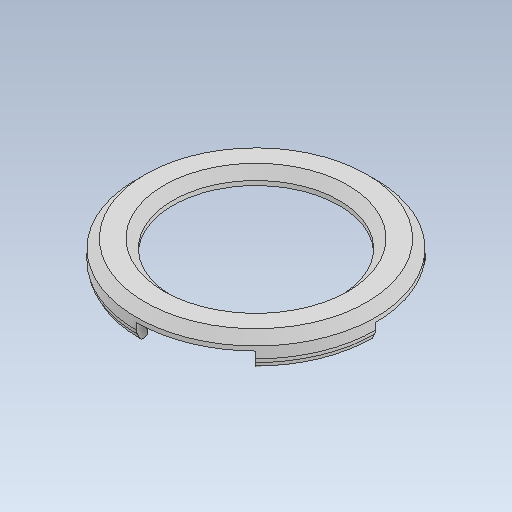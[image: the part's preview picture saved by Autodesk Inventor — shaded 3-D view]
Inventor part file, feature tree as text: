
AUTODESK INVENTOR PART (.ipt)
format: ipt  version: 2020 (Build 240168000, 168)  size: 195,584 bytes
history: native  units: mm
features: revolve x2, chamfer x2, sketch x2, other x1, pattern_circular x1
ambient origin geometry x8: Origin, YZ Plane, XZ Plane, XY Plane, X Axis, Y Axis, Z Axis, Center Point
bodies: Body1 (feature_tree)
feature tree (8):
  other  "Твердое тело1"
  revolve  "Вращение1"
  chamfer  "Фаска1"  Distance=19.0mm
  chamfer  "Фаска2"  Distance=27.3mm
  revolve  "Вращение2"
  pattern_circular  "Круговой массив1"  [2 undecoded]
  sketch  "Эскиз1"
  sketch  "Эскиз2"
note: 2 required parameter values undecoded (feature->parameter linkage not recoverable at this tier; creation-order binding heuristic only, values carry confidence <= 0.55)
